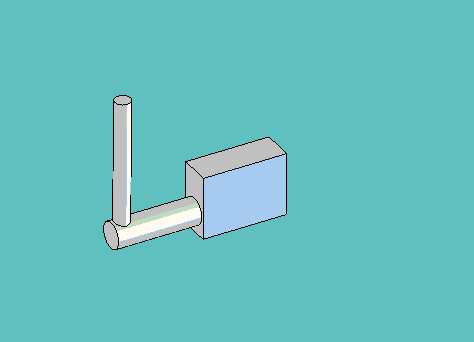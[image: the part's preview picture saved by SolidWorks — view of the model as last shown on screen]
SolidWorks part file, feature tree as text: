
SOLIDWORKS PART (.sldprt)
format: sldprt  version: not decoded by parser v0  size: 214,016 bytes
history: native  units: mm
features: sketch x3, extrude x3, material x1, plane x1 (+11 scaffold rows collapsed)
feature tree (19):
  scaffold x11  (default folders/planes/origin — collapsed)
  material  "Material <not specified>"
  sketch  "Sketch3"  dims[c1.D1=22.225mm c1.D2=25.4mm c2.D1=19.05mm c2.D3=22.225mm]
  extrude  "Extrude3"  Depth=9.525mm
  sketch  "Sketch4"  dims[D1=7.9375mm D2=6.35mm]
  extrude  "Extrude4"  Depth=25.4mm
  plane  "Plane1"
  sketch  "Sketch5"  dims[D1=4.7625mm D2=3.175mm]
  extrude  "Extrude5"  Depth=41.275mm
decode coverage: 6 of 6 modeling features carry decoded parameters
note: suppression state not decoded; provenance and decode notes live in map.json
